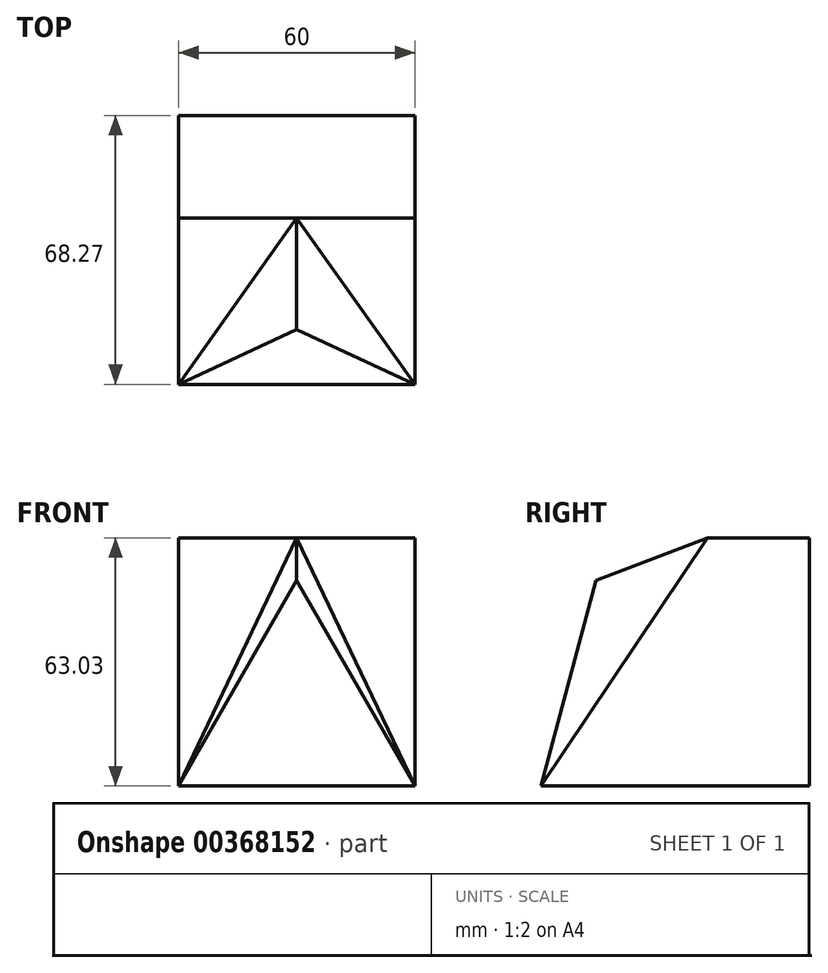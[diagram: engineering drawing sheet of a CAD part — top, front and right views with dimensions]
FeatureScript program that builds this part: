
annotation { "Feature Type Name" : "Feature", "Feature Type Description" : "" }
export const myFeature = defineFeature(function(context is Context, id is Id, definition is map)
    precondition{}
    {
        {
            var Q0;
            Q0=qCreatedBy(makeId("Right.planeOp"),FACE);
            var sketch = newSketch(context, id + "F0", { "sketchPlane" : qUnion([Q0])});
            skLineSegment(sketch, "E0", {"start": v(0, 0) * mm, "end": v(0, 63.03) * mm});
            skLineSegment(sketch, "E1", {"start": v(0, 63.03) * mm, "end": v(-25.99, 63.03) * mm});
            skLineSegment(sketch, "E2", {"start": v(-25.99, 63.03) * mm, "end": v(-68.27, 0) * mm});
            skLineSegment(sketch, "E3", {"start": v(-68.27, 0) * mm, "end": v(0, 0) * mm});
            skPoint(sketch, "E4", {"position": v(-54.3, 52.17) * mm});
            skSolve(sketch);
        }
        {
            var Q0;
            Q0=makeQuery(id+"F0.imprint","IMPRINT",FACE,{"disambiguationData":[TD([[makeQuery(id+"F0.imprint","IMPRINT",EDGE,{"derivedFrom":sQuery(id+"F0.wireOp",EDGE,"E0")}),1.0]])]});
            extrude(context, id + "F1", {"entities" : qUnion([Q0]), "endBound" : BoundingType.SYMMETRIC, "depth" : 60 * mm});
        }
        {
            var Q0;
            Q0=makeQuery(id+"F1.opExtrude","SWEPT_FACE",FACE,{"disambiguationData":[OSD([sQuery(id+"F0.wireOp",EDGE,"E2")])]});
            var sketch = newSketch(context, id + "F2", { "sketchPlane" : qUnion([Q0])});
            skLineSegment(sketch, "E5", {"start": v(-30, -38.03) * mm, "end": v(0, 37.87) * mm});
            skLineSegment(sketch, "E6", {"start": v(0, 37.87) * mm, "end": v(30, -38.03) * mm});
            skLineSegment(sketch, "E7", {"start": v(30, -38.03) * mm, "end": v(-30, -38.03) * mm});
            skSolve(sketch);
        }
        {
            var Q1;
            Q1=makeQuery(id+"F2.imprint","IMPRINT",FACE,{"disambiguationData":[TD([[makeQuery(id+"F2.imprint","IMPRINT",EDGE,{"derivedFrom":sQuery(id+"F2.wireOp",EDGE,"E5")}),-1.0]])]});
            var Q2;
            Q2=sQuery(id+"F0.wireOp",VERTEX,"E4");
            loft(context, id + "F3", {"operationType" : NewBodyOperationType.ADD, "sheetProfilesArray" : [{ "sheetProfileEntities" : qUnion([Q1]) }, { "sheetProfileEntities" : qUnion([Q2]) }]});
        }
    });
